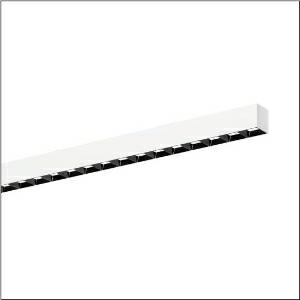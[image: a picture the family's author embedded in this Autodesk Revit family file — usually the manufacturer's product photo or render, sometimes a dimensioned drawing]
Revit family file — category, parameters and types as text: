
# Revit family: silica_r__21_51mx22dc4awb_3425
name_source: partatom
category: Lighting Fixtures
units: mm (PartAtom-declared; Revit-internal decimal feet)

## family parameters
Cut with Voids When Loaded = No
Host = Face
Light Source = No
Part Type = Normal
Room Calculation Point = No
Round Connector Dimension = Use Diameter
Shared = No

## types (1)
- --- (1 x LED, 10800 lm, 64.7 W, 4000K)
    Apparent Load = 65 VA
    CIE Flux Codes = 86 100 100 100 100
    Color Rendering = 80
    Color Temperature = 4000K
    Default Elevation = 1800 mm
    Description = Silica® 21, office luminaire, primary light control with darklight reflector, of PMMA, black, CAT 2 (L<= 3000cd/m²), light emission: direct distribution, primary light characteristic: symmetric, installation type: surface-mounted, LED, rated luminous flux: 10.800lm, luminous efficacy: 167lm/W, light colour: 840, colour temperature: 4000K, control gear: DALI 2, with terminal, 3+2-pole, max. 2.5mm², mains connection: 220..240V, AC, 50/60Hz, rated input power: 64.7W, luminaire housing, of aluminium, traffic white (RAL 9016), length: 3.004mm, width: 53mm, height: 53mm, protection rating (complete): IP20, insulation class (complete): insulation class I (protective earthing), certification: CE, permissible operating ambient temperature: 0..+35°C, standard: EN 50419, packaging unit: 1 piece
    Height = 53 mm
    Lamp = 1 x LED
    Lamp Light Flux = 10800 lm
    Lamp Power = 64.7 W
    Lamp count = 1
    Length = 3004 mm
    Luminous efficacy = 167 lm/W
    Manufacturer = Siteco
    ModVariant = No
    Model = 51MX22DC4AWB
    Mounting Place = Ceiling
    Mounting Type = Surface mounted
    Number of Poles = 1
    OnlyDefault = Yes
    Power Factor = 1
    Product Name = Silica® 21
    Product group = office luminaire | ceiling mounted
    ProductGroupID = 302
    Protection Class = Protection class I
    Protection Degree = IP 20
    RLX_Detail_Level = 1
    RLX_Emergency_Light_Flux = 0 lm
    RLX_Emergency_Type = 0
    RLX_Emergency_Type_DB = No
    RlxData = <blob elided: 61797 chars, md5=fc9a5f1d>
    Socket = socket
    Standby Power = 0 W
    System Light Flux = 10800 lm
    System Power = 65 W
    Type Comments = factory setting: luminous flux: 100 % | dim-lin: 254 | 366 mA
    Type Image = l_1335873.jpg
    URL = http://relux.com
    VarID = @adj_124882
    Voltage = 0 V
    Weight = 0.00 kg
    Width = 53 mm

## geometry (parser evidence)
native form markers: Blend x4, Sweep x12
no freeform markers — native parametric forms only
